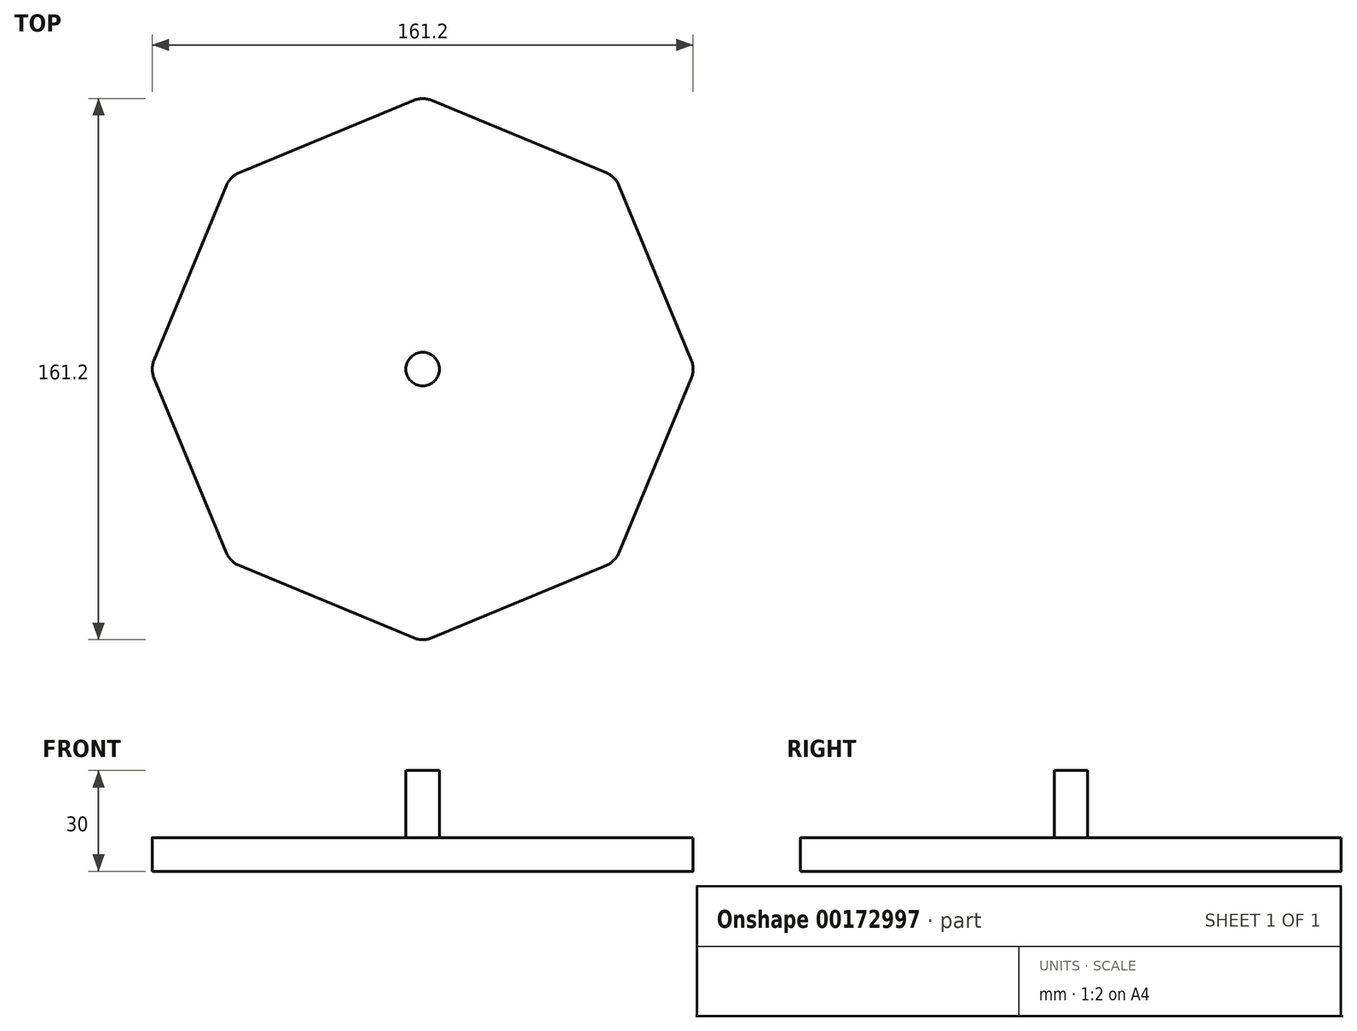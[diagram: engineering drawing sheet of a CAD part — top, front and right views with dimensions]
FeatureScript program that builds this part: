
annotation { "Feature Type Name" : "Feature", "Feature Type Description" : "" }
export const myFeature = defineFeature(function(context is Context, id is Id, definition is map)
    precondition{}
    {
        {
            var Q0;
            Q0=qCreatedBy(makeId("Top.planeOp"),FACE);
            var sketch = newSketch(context, id + "F0", { "sketchPlane" : qUnion([Q0])});
            skCircle(sketch, "E0.cCircle", {"center": v(0, 0) * mm, "radius": 75 * mm, "construction": true});
            skLineSegment(sketch, "E0.0", {"start": v(57.4, 57.4) * mm, "end": v(81.18, 0) * mm});
            skLineSegment(sketch, "E0.1", {"start": v(81.18, 0) * mm, "end": v(57.4, -57.4) * mm});
            skLineSegment(sketch, "E0.2", {"start": v(57.4, -57.4) * mm, "end": v(0, -81.18) * mm});
            skLineSegment(sketch, "E0.3", {"start": v(0, -81.18) * mm, "end": v(-57.4, -57.4) * mm});
            skLineSegment(sketch, "E0.4", {"start": v(-57.4, -57.4) * mm, "end": v(-81.18, 0) * mm});
            skLineSegment(sketch, "E0.5", {"start": v(-81.18, 0) * mm, "end": v(-57.4, 57.4) * mm});
            skLineSegment(sketch, "E0.6", {"start": v(-57.4, 57.4) * mm, "end": v(0, 81.18) * mm});
            skLineSegment(sketch, "E0.7", {"start": v(0, 81.18) * mm, "end": v(57.4, 57.4) * mm});
            skPoint(sketch, "E0.0.midPoint", {"position": v(69.3, 28.7) * mm});
            skSolve(sketch);
        }
        {
            var Q0;
            Q0 = qSketchRegion(id + "F0", true);
            extrude(context, id + "F1", {"entities" : qUnion([Q0]), "depth" : 10 * mm});
        }
        {
            var Q0;
            Q0=makeQuery(id+"F1.opExtrude","CAP_FACE",FACE,{"disambiguationData":[OSD([sQuery(id+"F0.wireOp",EDGE,"E0.0"),sQuery(id+"F0.wireOp",EDGE,"E0.1"),sQuery(id+"F0.wireOp",EDGE,"E0.2"),sQuery(id+"F0.wireOp",EDGE,"E0.3"),sQuery(id+"F0.wireOp",EDGE,"E0.4"),sQuery(id+"F0.wireOp",EDGE,"E0.5"),sQuery(id+"F0.wireOp",EDGE,"E0.6"),sQuery(id+"F0.wireOp",EDGE,"E0.7")])],"isStart":false});
            var sketch = newSketch(context, id + "F2", { "sketchPlane" : qUnion([Q0])});
            skCircle(sketch, "E1", {"center": v(0, 0) * mm, "radius": 5 * mm});
            skSolve(sketch);
        }
        {
            var Q0;
            Q0 = qSketchRegion(id + "F2", true);
            extrude(context, id + "F3", {"entities" : qUnion([Q0]), "operationType" : NewBodyOperationType.ADD, "depth" : 20 * mm});
        }
        {
            var Q0;
            Q0=makeQuery(id+"F1.opExtrude","SWEPT_EDGE",EDGE,{"disambiguationData":[OSD([sQuery(id+"F0.wireOp",EDGE,"E0.5"),sQuery(id+"F0.wireOp",EDGE,"E0.6")])]});
            var Q1;
            Q1=makeQuery(id+"F1.opExtrude","SWEPT_EDGE",EDGE,{"disambiguationData":[OSD([sQuery(id+"F0.wireOp",EDGE,"E0.4"),sQuery(id+"F0.wireOp",EDGE,"E0.5")])]});
            var Q2;
            Q2=makeQuery(id+"F1.opExtrude","SWEPT_EDGE",EDGE,{"disambiguationData":[OSD([sQuery(id+"F0.wireOp",EDGE,"E0.6"),sQuery(id+"F0.wireOp",EDGE,"E0.7")])]});
            var Q3;
            Q3=makeQuery(id+"F1.opExtrude","SWEPT_EDGE",EDGE,{"disambiguationData":[OSD([sQuery(id+"F0.wireOp",EDGE,"E0.3"),sQuery(id+"F0.wireOp",EDGE,"E0.4")])]});
            var Q4;
            Q4=makeQuery(id+"F1.opExtrude","SWEPT_EDGE",EDGE,{"disambiguationData":[OSD([sQuery(id+"F0.wireOp",EDGE,"E0.2"),sQuery(id+"F0.wireOp",EDGE,"E0.3")])]});
            var Q5;
            Q5=makeQuery(id+"F1.opExtrude","SWEPT_EDGE",EDGE,{"disambiguationData":[OSD([sQuery(id+"F0.wireOp",EDGE,"E0.1"),sQuery(id+"F0.wireOp",EDGE,"E0.2")])]});
            var Q6;
            Q6=makeQuery(id+"F1.opExtrude","SWEPT_EDGE",EDGE,{"disambiguationData":[OSD([sQuery(id+"F0.wireOp",EDGE,"E0.0"),sQuery(id+"F0.wireOp",EDGE,"E0.1")])]});
            var Q7;
            Q7=makeQuery(id+"F1.opExtrude","SWEPT_EDGE",EDGE,{"disambiguationData":[OSD([sQuery(id+"F0.wireOp",EDGE,"E0.0"),sQuery(id+"F0.wireOp",EDGE,"E0.7")])]});
            fillet(context, id + "F4", {"entities" : qUnion([Q0, Q1, Q2, Q3, Q4, Q5, Q6, Q7]), "radius" : 7 * mm, "tangentPropagation" : true, "allowEdgeOverflow" : false});
        }
    });
